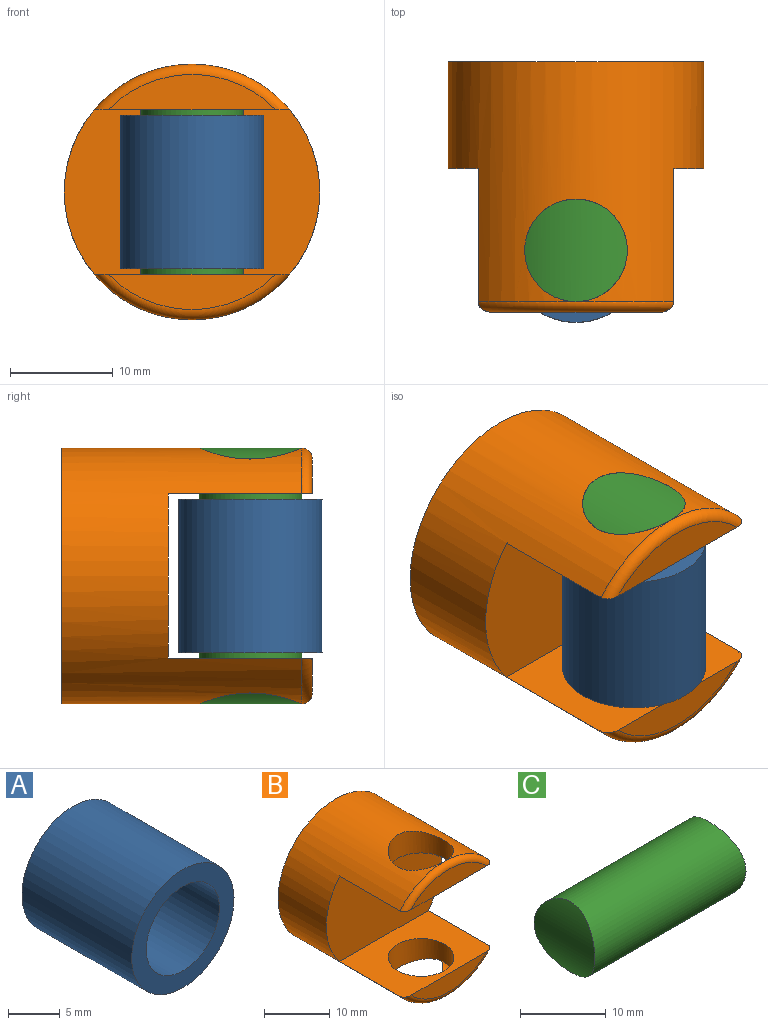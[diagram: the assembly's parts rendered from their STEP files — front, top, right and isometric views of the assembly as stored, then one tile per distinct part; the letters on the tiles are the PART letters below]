
ASSEMBLY  parts=3 mates=2
PART A: 4 faces, bbox 14x15x14 mm
  f0: cylinder r=5mm len=15mm, axis (0,1,0), area 471.2mm2, adj f2,f3
  f1: cylinder r=7mm len=15mm, axis (0,1,0), area 659.7mm2, adj f2,f3
  f2: plane 14x14mm, normal (0,-1,0), area 75.4mm2, adj f0,f1
  f3: plane 14x14mm, normal (0,1,0), area 75.4mm2, adj f0,f1
PART B: 11 faces, bbox 24.9x24.4x27 mm
  f0: plane 24.9x16mm, normal (0,-1,0), area 369mm2, adj f2,f5,f8
  f1: plane 16.38x3.45mm, normal (0,-1,0), area 39mm2, adj f2,f9
  f2: plane 19.08x14mm, normal (0,0,-1), area 188mm2, adj f0,f1,f3,f8,f9
  f3: cylinder r=5mm len=10mm, axis (0,0,1), area 123.5mm2, adj f2,f8
  f4: plane 16.38x3.45mm, normal (0,-1,0), area 39mm2, adj f5,f10
  f5: plane 19.08x14mm, normal (0,0,1), area 188mm2, adj f0,f4,f6,f8,f10
  f6: cylinder r=5mm len=10mm, axis (0,0,1), area 123.5mm2, adj f5,f8
  f7: plane 24.9x24.9mm, normal (0,1,0), area 487mm2, adj f8
  f8: cylinder r=12.45mm len=24.9mm, axis (0,1,0), area 1218.4mm2, adj f0,f2,f3,f5,f6,f7,f9,f10
  f9: torus R=11.45mm, axis (0,-1,0), area 32.2mm2, adj f1,f2,f8
  f10: torus R=11.45mm, axis (0,-1,0), area 32.2mm2, adj f4,f5,f8
PART C: 3 faces, bbox 24.9x10x10 mm
  f0: cylinder r=5mm len=24.9mm, axis (-1,0,0), area 749.7mm2, adj f1,f2
  f1: cylinder r=12.45mm len=10mm, axis (0,-1,0), area 80.3mm2, adj f0
  f2: cylinder r=12.45mm len=10mm, axis (0,-1,0), area 80.2mm2, adj f0
PLACE A rot(axis=(1,0,0),90deg) t=(-15.45,-16.82,3.92)mm
PLACE B t=(-15.45,1.58,-3.58)mm
PLACE C rot(axis=(0,1,0),90deg) t=(-15.45,-11.82,-3.58)mm
MATE fastened C.f0 <-> B.f3  axis (0,0,1) through (-15.45,-16.82,9.02)mm
MATE revolute A.f0 <-> C.f0  axis (0,0,1) through (-15.45,-16.82,-3.58)mm
